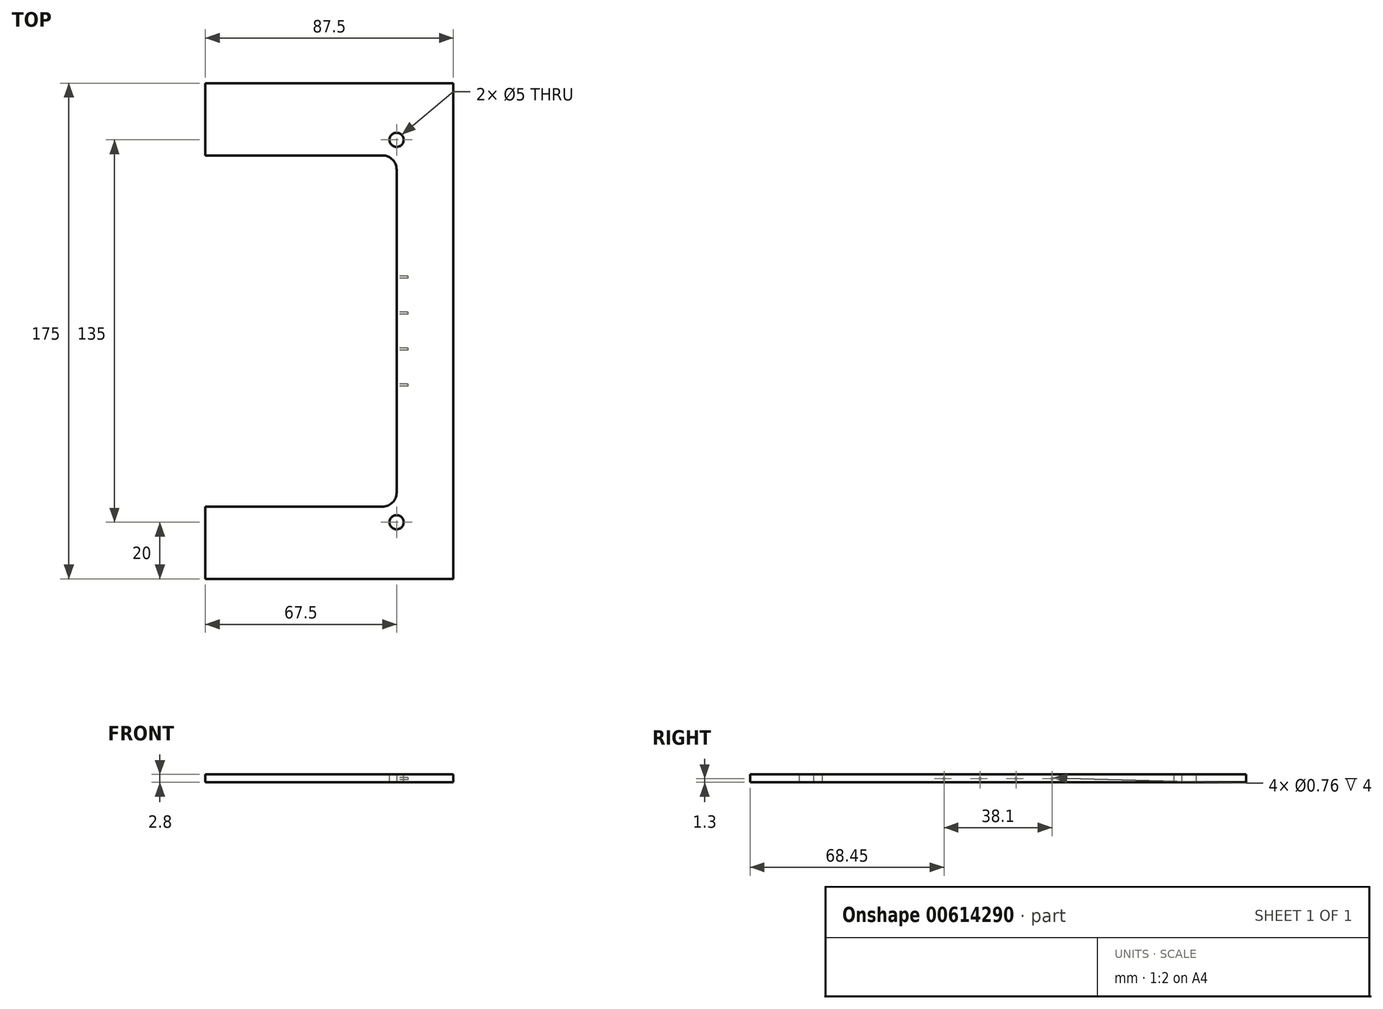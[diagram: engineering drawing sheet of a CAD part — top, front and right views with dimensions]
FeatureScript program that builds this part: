
annotation { "Feature Type Name" : "Feature", "Feature Type Description" : "" }
export const myFeature = defineFeature(function(context is Context, id is Id, definition is map)
    precondition{}
    {
        {
            var Q0;
            Q0=qCreatedBy(makeId("Top.planeOp"),FACE);
            var sketch = newSketch(context, id + "F0", { "sketchPlane" : qUnion([Q0])});
            skLineSegment(sketch, "E0.bottom", {"start": v(0, 0) * mm, "end": v(87.5, 0) * mm});
            skLineSegment(sketch, "E0.top", {"start": v(0, 175) * mm, "end": v(87.5, 175) * mm});
            skLineSegment(sketch, "E0.left", {"start": v(0, 0) * mm, "end": v(0, 25.5) * mm});
            skLineSegment(sketch, "E0.right", {"start": v(87.5, 0) * mm, "end": v(87.5, 175) * mm});
            skLineSegment(sketch, "E1.bottom", {"start": v(0, 149.5) * mm, "end": v(67.5, 149.5) * mm});
            skLineSegment(sketch, "E1.top", {"start": v(0, 25.5) * mm, "end": v(62.5, 25.5) * mm});
            skLineSegment(sketch, "E1.right", {"start": v(67.5, 144.5) * mm, "end": v(67.5, 30.5) * mm});
            skLineSegment(sketch, "E2.top", {"start": v(0, 149.5) * mm, "end": v(62.5, 149.5) * mm});
            skLineSegment(sketch, "E2.left", {"start": v(0, 149.5) * mm, "end": v(0, 149.5) * mm});
            skLineSegment(sketch, "E2.right", {"start": v(67.5, 149.5) * mm, "end": v(67.5, 149.5) * mm});
            skLineSegment(sketch, "E3.trimOffspring", {"start": v(0, 149.5) * mm, "end": v(0, 175) * mm});
            skPoint(sketch, "E4.visualSharp", {"position": v(67.5, 149.5) * mm});
            skArc(sketch, "E4.filletArc", {"start": v(67.5, 144.5) * mm, "mid": v(66.04, 148.04) * mm, "end": v(62.5, 149.5) * mm});
            skPoint(sketch, "E5.visualSharp", {"position": v(67.5, 25.5) * mm});
            skArc(sketch, "E5.filletArc", {"start": v(62.5, 25.5) * mm, "mid": v(66.04, 26.96) * mm, "end": v(67.5, 30.5) * mm});
            skSolve(sketch);
        }
        {
            var Q0;
            Q0=makeQuery(id+"F0.imprint","IMPRINT",FACE,{"disambiguationData":[TD([[makeQuery(id+"F0.imprint","IMPRINT",EDGE,{"derivedFrom":sQuery(id+"F0.wireOp",EDGE,"E0.bottom")}),1.0]])]});
            extrude(context, id + "F1", {"entities" : qUnion([Q0]), "depth" : 2.8 * mm, "offsetDistance" : 25 * mm});
        }
        {
            var Q0;
            Q0=makeQuery(id+"F1.opExtrude","SWEPT_FACE",FACE,{"disambiguationData":[OSD([sQuery(id+"F0.wireOp",EDGE,"E1.right")])]});
            var sketch = newSketch(context, id + "F2", { "sketchPlane" : qUnion([Q0])});
            skLineSegment(sketch, "E6", {"start": v(-87.5, 2.8) * mm, "end": v(-87.5, 0) * mm, "construction": true});
            skCircle(sketch, "E7", {"center": v(-93.85, 1.3) * mm, "radius": 0.38 * mm});
            skCircle(sketch, "E8", {"center": v(-106.55, 1.3) * mm, "radius": 0.38 * mm});
            skCircle(sketch, "E9", {"center": v(-81.15, 1.3) * mm, "radius": 0.38 * mm});
            skCircle(sketch, "E10", {"center": v(-68.45, 1.3) * mm, "radius": 0.38 * mm});
            skSolve(sketch);
        }
        {
            var Q0;
            Q0=makeQuery(id+"F2.imprint","IMPRINT",FACE,{"disambiguationData":[TD([[makeQuery(id+"F2.imprint","IMPRINT",EDGE,{"derivedFrom":sQuery(id+"F2.wireOp",EDGE,"E8")}),1.0]])]});
            var Q1;
            Q1=makeQuery(id+"F2.imprint","IMPRINT",FACE,{"disambiguationData":[TD([[makeQuery(id+"F2.imprint","IMPRINT",EDGE,{"derivedFrom":sQuery(id+"F2.wireOp",EDGE,"E7")}),1.0]])]});
            var Q2;
            Q2=makeQuery(id+"F2.imprint","IMPRINT",FACE,{"disambiguationData":[TD([[makeQuery(id+"F2.imprint","IMPRINT",EDGE,{"derivedFrom":sQuery(id+"F2.wireOp",EDGE,"E9")}),1.0]])]});
            var Q3;
            Q3=makeQuery(id+"F2.imprint","IMPRINT",FACE,{"disambiguationData":[TD([[makeQuery(id+"F2.imprint","IMPRINT",EDGE,{"derivedFrom":sQuery(id+"F2.wireOp",EDGE,"E10")}),1.0]])]});
            extrude(context, id + "F3", {"entities" : qUnion([Q0, Q1, Q2, Q3]), "operationType" : NewBodyOperationType.REMOVE, "oppositeDirection" : true, "depth" : 4 * mm, "offsetDistance" : 25 * mm});
        }
        {
            var Q0;
            Q0=makeQuery(id+"F1.opExtrude","CAP_FACE",FACE,{"disambiguationData":[OSD([sQuery(id+"F0.wireOp",EDGE,"E0.bottom"),sQuery(id+"F0.wireOp",EDGE,"E0.top"),sQuery(id+"F0.wireOp",EDGE,"E0.left"),sQuery(id+"F0.wireOp",EDGE,"E0.right"),sQuery(id+"F0.wireOp",EDGE,"E1.top"),sQuery(id+"F0.wireOp",EDGE,"E1.right"),sQuery(id+"F0.wireOp",EDGE,"E2.top"),sQuery(id+"F0.wireOp",EDGE,"E3.trimOffspring"),sQuery(id+"F0.wireOp",EDGE,"E4.filletArc"),sQuery(id+"F0.wireOp",EDGE,"E5.filletArc")])],"isStart":false});
            var sketch = newSketch(context, id + "F4", { "sketchPlane" : qUnion([Q0])});
            skCircle(sketch, "E11", {"center": v(67.5, 155) * mm, "radius": 2.5 * mm});
            skCircle(sketch, "E12", {"center": v(67.5, 20) * mm, "radius": 2.5 * mm});
            skSolve(sketch);
        }
        {
            var Q0;
            Q0=makeQuery(id+"F4.imprint","IMPRINT",FACE,{"disambiguationData":[TD([[makeQuery(id+"F4.imprint","IMPRINT",EDGE,{"derivedFrom":sQuery(id+"F4.wireOp",EDGE,"E11")}),1.0]])]});
            var Q1;
            Q1=makeQuery(id+"F4.imprint","IMPRINT",FACE,{"disambiguationData":[TD([[makeQuery(id+"F4.imprint","IMPRINT",EDGE,{"derivedFrom":sQuery(id+"F4.wireOp",EDGE,"E12")}),1.0]])]});
            extrude(context, id + "F5", {"entities" : qUnion([Q0, Q1]), "operationType" : NewBodyOperationType.REMOVE, "endBound" : BoundingType.THROUGH_ALL, "oppositeDirection" : true, "depth" : 25 * mm, "offsetDistance" : 25 * mm});
        }
    });
